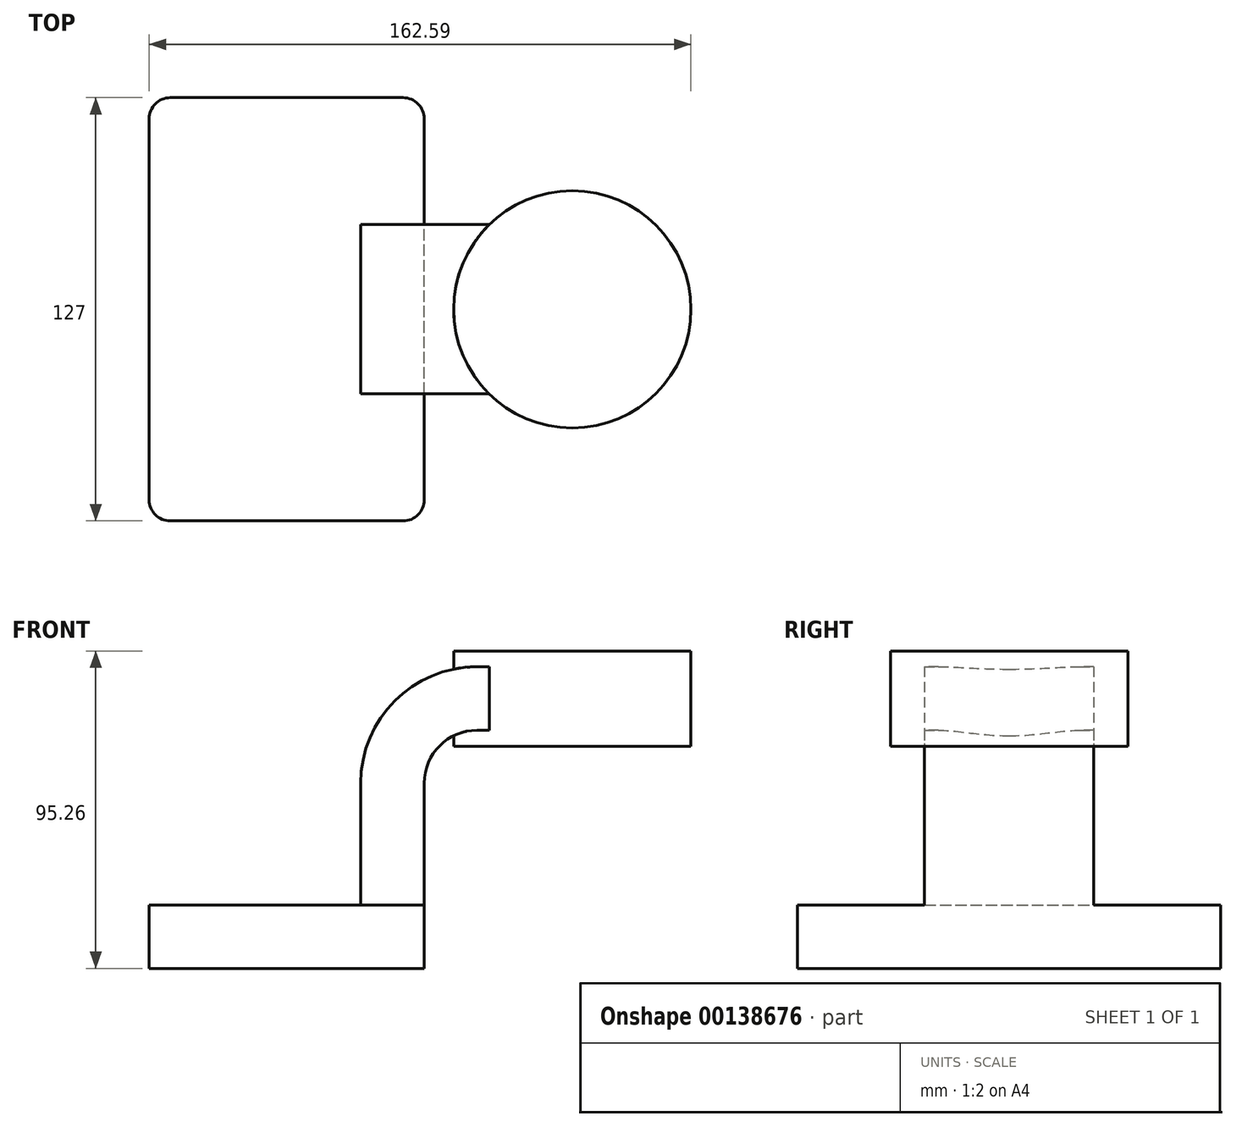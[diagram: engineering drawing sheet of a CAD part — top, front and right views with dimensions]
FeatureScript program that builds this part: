
annotation { "Feature Type Name" : "Feature", "Feature Type Description" : "" }
export const myFeature = defineFeature(function(context is Context, id is Id, definition is map)
    precondition{}
    {
        {
            var Q0;
            Q0=qCreatedBy(makeId("Front.planeOp"),FACE);
            var sketch = newSketch(context, id + "F0", { "sketchPlane" : qUnion([Q0])});
            skLineSegment(sketch, "E0.bottom", {"start": v(41.28, -9.52) * mm, "end": v(-41.28, -9.53) * mm});
            skLineSegment(sketch, "E0.top", {"start": v(41.27, 9.53) * mm, "end": v(-41.28, 9.53) * mm});
            skLineSegment(sketch, "E0.left", {"start": v(41.28, -9.52) * mm, "end": v(41.28, 9.53) * mm});
            skLineSegment(sketch, "E0.right", {"start": v(-41.28, -9.53) * mm, "end": v(-41.28, 9.53) * mm});
            skPoint(sketch, "E0.middle", {"position": v(0, 0) * mm});
            skLineSegment(sketch, "E1.bottom", {"start": v(70.52, 57.15) * mm, "end": v(121.32, 57.15) * mm});
            skLineSegment(sketch, "E1.top", {"start": v(70.52, 85.73) * mm, "end": v(121.32, 85.73) * mm});
            skLineSegment(sketch, "E1.left", {"start": v(70.52, 57.15) * mm, "end": v(70.52, 85.73) * mm});
            skLineSegment(sketch, "E1.right", {"start": v(121.32, 57.15) * mm, "end": v(121.32, 85.73) * mm});
            skLineSegment(sketch, "E2", {"start": v(41.27, 9.53) * mm, "end": v(41.27, 46.05) * mm});
            skArc(sketch, "E3", {"start": v(41.27, 46.05) * mm, "mid": v(45.92, 57.28) * mm, "end": v(57.15, 61.93) * mm});
            skLineSegment(sketch, "E4", {"start": v(57.15, 61.93) * mm, "end": v(85.72, 61.93) * mm});
            skLineSegment(sketch, "E5.0", {"start": v(57.15, 80.98) * mm, "end": v(85.72, 80.98) * mm});
            skArc(sketch, "E5.1", {"start": v(22.23, 46.05) * mm, "mid": v(32.45, 70.75) * mm, "end": v(57.15, 80.98) * mm});
            skLineSegment(sketch, "E5.2", {"start": v(22.22, 9.53) * mm, "end": v(22.22, 46.05) * mm});
            skLineSegment(sketch, "E6", {"start": v(85.72, 61.93) * mm, "end": v(85.72, 80.98) * mm});
            skFitSpline(sketch, "E7", {"points": [v(-41.28, 9.53) * mm, v(57.15, 80.98) * mm], "startDerivative": vector(25.88, 119.13) * mm, "endDerivative": vector(122.37, -0.98) * mm});
            skLineSegment(sketch, "E8", {"start": v(85.72, 61.93) * mm, "end": v(85.72, 57.15) * mm});
            skLineSegment(sketch, "E9", {"start": v(85.72, 80.98) * mm, "end": v(85.72, 85.73) * mm});
            skSolve(sketch);
        }
        {
            var Q0;
            Q0=makeQuery(id+"F0.imprint","IMPRINT",FACE,{"disambiguationData":[TD([[makeQuery(id+"F0.imprint","IMPRINT",EDGE,{"derivedFrom":sQuery(id+"F0.wireOp",EDGE,"E0.bottom")}),-1.0]])]});
            extrude(context, id + "F1", {"entities" : qUnion([Q0]), "endBound" : BoundingType.SYMMETRIC, "depth" : 127 * mm});
        }
        {
            var Q0;
            {var subQ1=sQuery(id+"F0.wireOp",EDGE,"E2");Q0=makeQuery(id+"F0.imprint","IMPRINT",FACE,{"disambiguationData":[TD([[makeQuery(id+"F0.imprint","IMPRINT",EDGE,{"derivedFrom":subQ1}),1.0]])]});}
            var Q1;
            {var subQ5=sQuery(id+"F0.wireOp",EDGE,"E6");Q1=makeQuery(id+"F0.imprint","IMPRINT",FACE,{"disambiguationData":[TD([[makeQuery(id+"F0.imprint","IMPRINT",EDGE,{"derivedFrom":subQ5}),1.0]])]});}
            extrude(context, id + "F2", {"entities" : qUnion([Q0, Q1]), "operationType" : NewBodyOperationType.ADD, "endBound" : BoundingType.SYMMETRIC, "depth" : 50.8 * mm});
        }
        {
            var Q0;
            Q0=makeQuery(id+"F0.imprint","IMPRINT",FACE,{"disambiguationData":[TD([[makeQuery(id+"F0.imprint","IMPRINT",EDGE,{"derivedFrom":sQuery(id+"F0.wireOp",EDGE,"E5.1")}),1.0]])]});
            extrude(context, id + "F3", {"entities" : qUnion([Q0]), "operationType" : NewBodyOperationType.ADD, "endBound" : BoundingType.SYMMETRIC, "depth" : 15.88 * mm});
        }
        {
            var Q0;
            {var subQ0=sQuery(id+"F0.wireOp",EDGE,"E1.right");Q0=makeQuery(id+"F0.imprint","IMPRINT",FACE,{"disambiguationData":[TD([[makeQuery(id+"F0.imprint","IMPRINT",EDGE,{"derivedFrom":subQ0}),1.0]])]});}
            var Q1;
            Q1=sQuery(id+"F0.wireOp",EDGE,"E6");
            revolve(context, id + "F4", {"operationType" : NewBodyOperationType.ADD, "entities" : qUnion([Q0]), "axis" : qUnion([Q1]), "revolveType" : RevolveType.FULL});
        }
        {
            var Q0;
            Q0=makeQuery(id+"F1.opExtrude","CAP_EDGE",EDGE,{"disambiguationData":[OSD([sQuery(id+"F0.wireOp",EDGE,"E0.left")])],"isStart":false});
            var Q1;
            Q1=makeQuery(id+"F1.opExtrude","CAP_EDGE",EDGE,{"disambiguationData":[OSD([sQuery(id+"F0.wireOp",EDGE,"E0.right")])],"isStart":false});
            var Q2;
            Q2=makeQuery(id+"F1.opExtrude","CAP_EDGE",EDGE,{"disambiguationData":[OSD([sQuery(id+"F0.wireOp",EDGE,"E0.right")])],"isStart":true});
            var Q3;
            Q3=makeQuery(id+"F1.opExtrude","CAP_EDGE",EDGE,{"disambiguationData":[OSD([sQuery(id+"F0.wireOp",EDGE,"E0.left")])],"isStart":true});
            fillet(context, id + "F5", {"entities" : qUnion([Q0, Q1, Q2, Q3]), "radius" : 6.35 * mm, "tangentPropagation" : true, "allowEdgeOverflow" : false});
        }
    });
